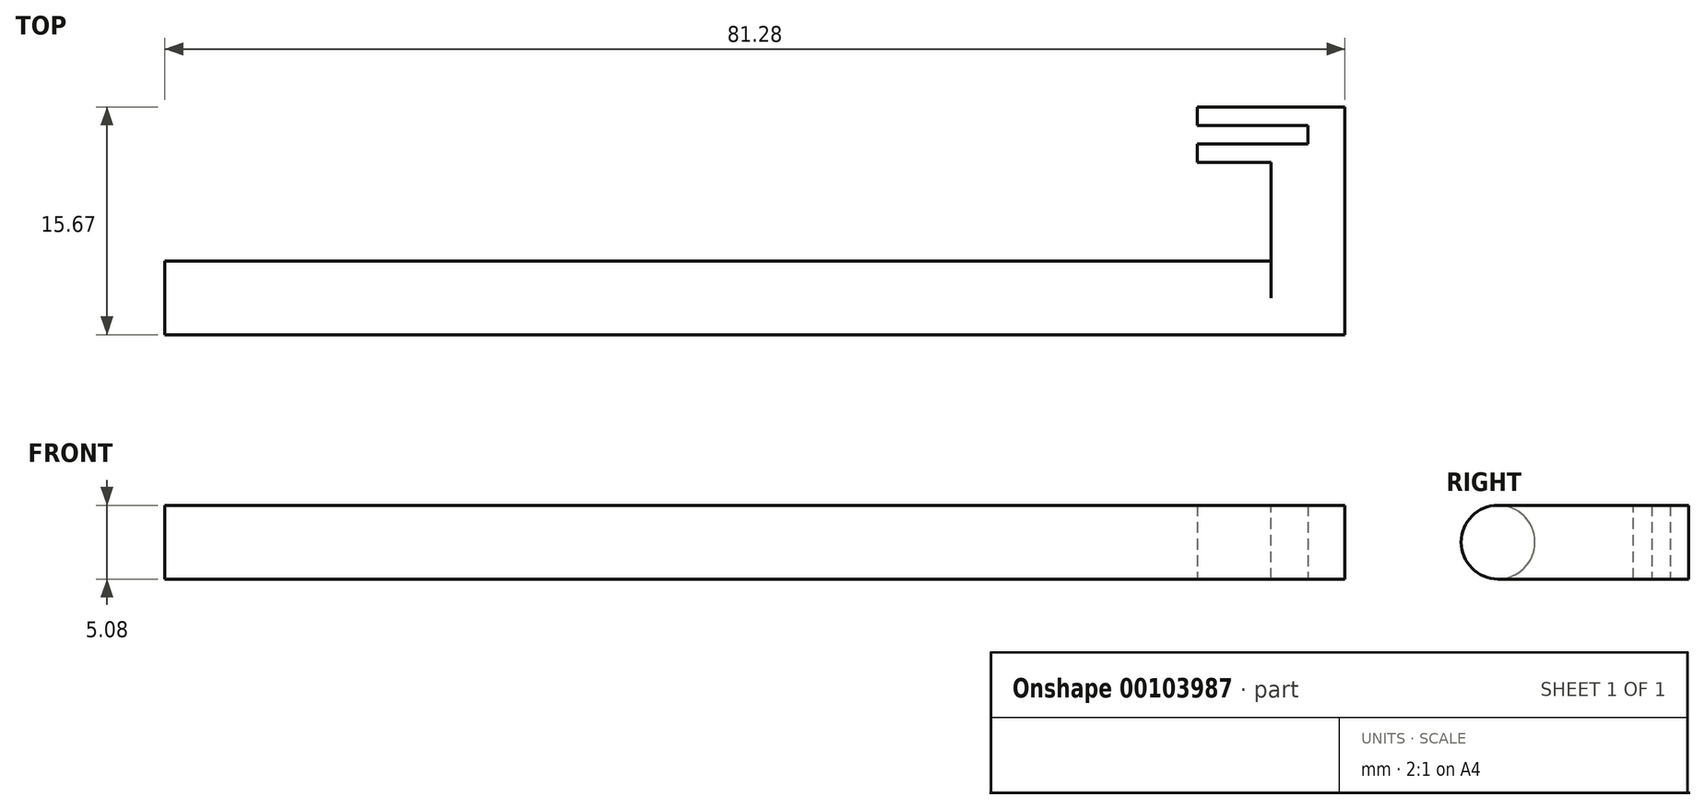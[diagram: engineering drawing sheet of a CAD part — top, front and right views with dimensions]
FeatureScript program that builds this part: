
annotation { "Feature Type Name" : "Feature", "Feature Type Description" : "" }
export const myFeature = defineFeature(function(context is Context, id is Id, definition is map)
    precondition{}
    {
        {
            var Q0;
            Q0=qCreatedBy(makeId("Right.planeOp"),FACE);
            var sketch = newSketch(context, id + "F0", { "sketchPlane" : qUnion([Q0])});
            skCircle(sketch, "E0", {"center": v(-37.06, 39.93) * mm, "radius": 2.54 * mm});
            skSolve(sketch);
        }
        {
            var Q0;
            Q0 = qSketchRegion(id + "F0", true);
            extrude(context, id + "F1", {"entities" : qUnion([Q0]), "depth" : 76.2 * mm});
        }
        {
            var Q0;
            Q0=makeQuery(id+"F1.opExtrude","CAP_FACE",FACE,{"disambiguationData":[OSD([sQuery(id+"F0.wireOp",EDGE,"E0")])],"isStart":false});
            var sketch = newSketch(context, id + "F2", { "sketchPlane" : qUnion([Q0])});
            skLineSegment(sketch, "E1", {"start": v(-37.06, 39.93) * mm, "end": v(-37.06, 42.47) * mm});
            skLineSegment(sketch, "E2", {"start": v(-37.06, 42.47) * mm, "end": v(-27.74, 42.47) * mm});
            skLineSegment(sketch, "E3", {"start": v(-37.06, 39.93) * mm, "end": v(-37.06, 37.4) * mm});
            skLineSegment(sketch, "E4", {"start": v(-37.06, 37.4) * mm, "end": v(-27.74, 37.4) * mm});
            skLineSegment(sketch, "E5", {"start": v(-27.74, 37.4) * mm, "end": v(-27.74, 42.47) * mm});
            skSolve(sketch);
        }
        {
            var Q0;
            {var subQ0=sQuery(id+"F2.wireOp",EDGE,"E2");Q0=makeQuery(id+"F2.imprint","IMPRINT",FACE,{"disambiguationData":[TD([[makeQuery(id+"F2.imprint","IMPRINT",EDGE,{"derivedFrom":subQ0}),-1.0]])]});}
            var Q1;
            {var subQ0=sQuery(id+"F2.wireOp",EDGE,"E1");Q1=makeQuery(id+"F2.imprint","IMPRINT",FACE,{"disambiguationData":[TD([[makeQuery(id+"F2.imprint","IMPRINT",EDGE,{"derivedFrom":subQ0}),-1.0]])]});}
            var Q2;
            {var subQ0=sQuery(id+"F2.wireOp",EDGE,"E1");Q2=makeQuery(id+"F2.imprint","IMPRINT",FACE,{"disambiguationData":[TD([[makeQuery(id+"F2.imprint","IMPRINT",EDGE,{"derivedFrom":subQ0}),1.0]])]});}
            extrude(context, id + "F3", {"entities" : qUnion([Q0, Q1, Q2]), "operationType" : NewBodyOperationType.ADD, "depth" : 5.08 * mm});
        }
        {
            var Q0;
            Q0=makeQuery(id+"F3.opExtrude","SWEPT_FACE",FACE,{"disambiguationData":[OSD([sQuery(id+"F2.wireOp",EDGE,"E5")])]});
            var sketch = newSketch(context, id + "F4", { "sketchPlane" : qUnion([Q0])});
            skLineSegment(sketch, "E6", {"start": v(-76.2, 42.47) * mm, "end": v(-71.12, 42.47) * mm});
            skLineSegment(sketch, "E7", {"start": v(-71.12, 42.47) * mm, "end": v(-71.12, 37.4) * mm});
            skLineSegment(sketch, "E8", {"start": v(-71.12, 37.4) * mm, "end": v(-76.2, 37.4) * mm});
            skLineSegment(sketch, "E9", {"start": v(-78.74, 42.47) * mm, "end": v(-78.74, 37.4) * mm});
            skSolve(sketch);
        }
        {
            var Q0;
            Q0=makeQuery(id+"F4.imprint","IMPRINT",FACE,{"disambiguationData":[TD([[makeQuery(id+"F4.imprint","IMPRINT",EDGE,{"derivedFrom":sQuery(id+"F4.wireOp",EDGE,"E6")}),-1.0]])]});
            var Q1;
            {var subQ0=sQuery(id+"F4.wireOp",EDGE,"E9");Q1=makeQuery(id+"F4.imprint","IMPRINT",FACE,{"disambiguationData":[TD([[makeQuery(id+"F4.imprint","IMPRINT",EDGE,{"derivedFrom":subQ0}),1.0]])]});}
            extrude(context, id + "F5", {"entities" : qUnion([Q0, Q1]), "operationType" : NewBodyOperationType.ADD, "depth" : 1.27 * mm});
        }
        {
            var Q0;
            Q0=makeQuery(id+"F3.opExtrude","SWEPT_FACE",FACE,{"disambiguationData":[OSD([sQuery(id+"F2.wireOp",EDGE,"E5")])]});
            extrude(context, id + "F6", {"entities" : qUnion([Q0]), "operationType" : NewBodyOperationType.ADD, "depth" : 3.8 * mm});
        }
        {
            var Q0;
            Q0=makeQuery(id+"F6.opExtrude","SWEPT_FACE",FACE,{"disambiguationData":[OSD([sQuery(id+"F4.wireOp",EDGE,"E9")])]});
            var sketch = newSketch(context, id + "F7", { "sketchPlane" : qUnion([Q0])});
            skLineSegment(sketch, "E10", {"start": v(25.2, 42.47) * mm, "end": v(25.2, 37.4) * mm});
            skSolve(sketch);
        }
        {
            var Q0;
            {var subQ0=sQuery(id+"F7.wireOp",EDGE,"E10");Q0=makeQuery(id+"F7.imprint","IMPRINT",FACE,{"disambiguationData":[TD([[makeQuery(id+"F7.imprint","IMPRINT",EDGE,{"derivedFrom":subQ0}),-1.0]])]});}
            extrude(context, id + "F8", {"entities" : qUnion([Q0]), "operationType" : NewBodyOperationType.ADD, "depth" : 7.62 * mm});
        }
    });
